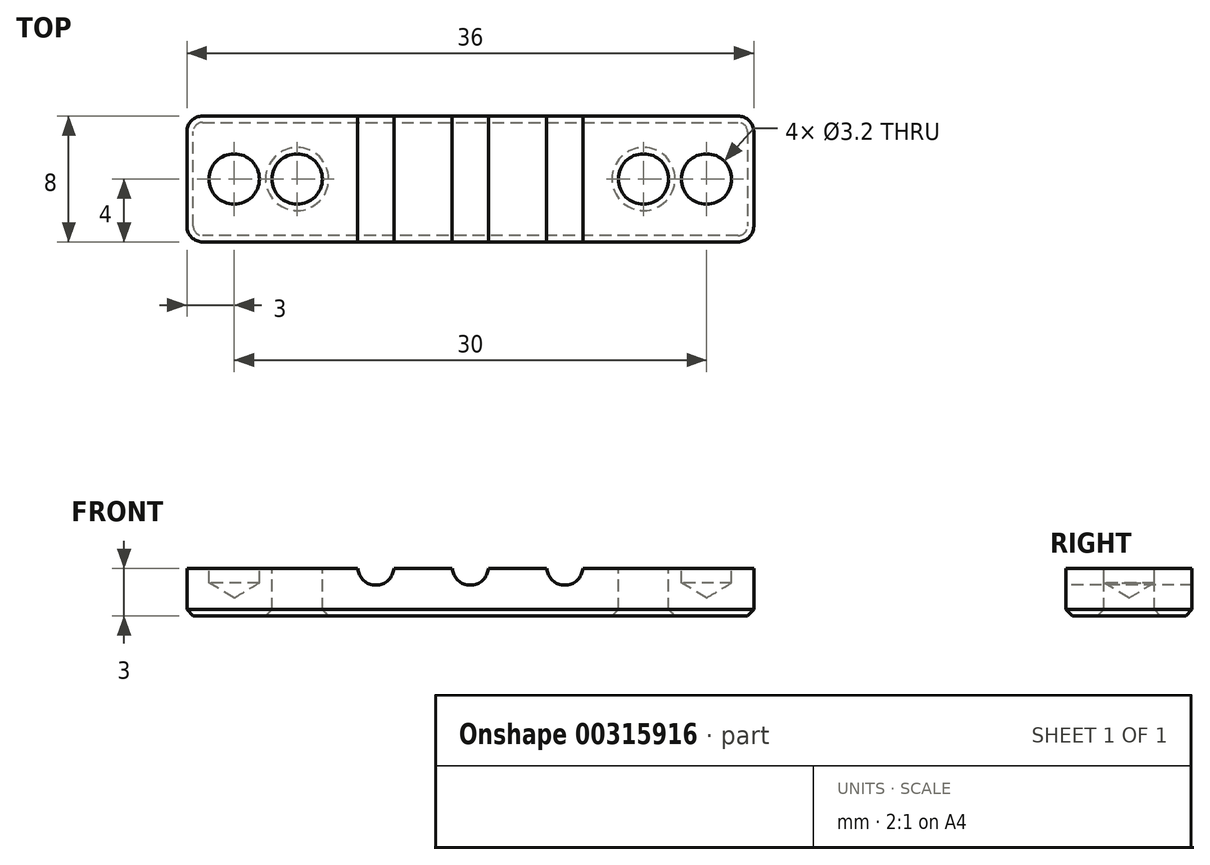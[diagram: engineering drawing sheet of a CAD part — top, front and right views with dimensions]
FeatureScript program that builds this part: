
annotation { "Feature Type Name" : "Feature", "Feature Type Description" : "" }
export const myFeature = defineFeature(function(context is Context, id is Id, definition is map)
    precondition{}
    {
        {
            var Q0;
            Q0=qCreatedBy(makeId("Top.planeOp"),FACE);
            var sketch = newSketch(context, id + "F0", { "sketchPlane" : qUnion([Q0])});
            skLineSegment(sketch, "E0.bottom", {"start": v(3, 4) * mm, "end": v(-3, 4) * mm});
            skLineSegment(sketch, "E0.top", {"start": v(3, -4) * mm, "end": v(-3, -4) * mm});
            skLineSegment(sketch, "E0.left", {"start": v(3, 4) * mm, "end": v(3, -4) * mm});
            skLineSegment(sketch, "E0.right", {"start": v(-3, 4) * mm, "end": v(-3, -4) * mm});
            skPoint(sketch, "E0.middle", {"position": v(0, 0) * mm});
            skLineSegment(sketch, "E1.bottom", {"start": v(33, 4) * mm, "end": v(27, 4) * mm});
            skLineSegment(sketch, "E1.top", {"start": v(33, -4) * mm, "end": v(27, -4) * mm});
            skLineSegment(sketch, "E1.left", {"start": v(33, 4) * mm, "end": v(33, -4) * mm});
            skLineSegment(sketch, "E1.right", {"start": v(27, 4) * mm, "end": v(27, -4) * mm});
            skPoint(sketch, "E1.middle", {"position": v(30, 0) * mm});
            skLineSegment(sketch, "E2", {"start": v(3, 4) * mm, "end": v(27, 4) * mm});
            skLineSegment(sketch, "E3", {"start": v(3, -4) * mm, "end": v(27, -4) * mm});
            skLineSegment(sketch, "E4", {"start": v(9, 4) * mm, "end": v(9, -4) * mm, "construction": true});
            skLineSegment(sketch, "E5.1.0.0", {"start": v(15, 4) * mm, "end": v(15, -4) * mm, "construction": true});
            skLineSegment(sketch, "E5.2.0.0", {"start": v(21, 4) * mm, "end": v(21, -4) * mm, "construction": true});
            skLineSegment(sketch, "E5.direction1", {"start": v(9, -4) * mm, "end": v(15, -4) * mm, "construction": true});
            skPoint(sketch, "E6", {"position": v(4, 0) * mm});
            skPoint(sketch, "E6.positionSnap0", {"position": v(3, 0) * mm});
            skPoint(sketch, "E7", {"position": v(26, 0) * mm});
            skPoint(sketch, "E7.positionSnap0", {"position": v(27, 0) * mm});
            skSolve(sketch);
        }
        {
            var Q0;
            Q0=makeQuery(id+"F0.imprint","IMPRINT",FACE,{"disambiguationData":[TD([[makeQuery(id+"F0.imprint","IMPRINT",EDGE,{"derivedFrom":sQuery(id+"F0.wireOp",EDGE,"E0.bottom")}),1.0]])]});
            var Q1;
            Q1=makeQuery(id+"F0.imprint","IMPRINT",FACE,{"disambiguationData":[TD([[makeQuery(id+"F0.imprint","IMPRINT",EDGE,{"derivedFrom":sQuery(id+"F0.wireOp",EDGE,"E0.left")}),1.0]])]});
            var Q2;
            Q2=makeQuery(id+"F0.imprint","IMPRINT",FACE,{"disambiguationData":[TD([[makeQuery(id+"F0.imprint","IMPRINT",EDGE,{"derivedFrom":sQuery(id+"F0.wireOp",EDGE,"E1.bottom")}),1.0]])]});
            extrude(context, id + "F1", {"entities" : qUnion([Q0, Q1, Q2]), "oppositeDirection" : true, "depth" : 3.1 * mm});
        }
        {
            var Q0;
            Q0=sQuery(id+"F0.wireOp",VERTEX,"E6");
            var Q1;
            Q1=sQuery(id+"F0.wireOp",VERTEX,"E7");
            var Q2;
            Q2=makeQuery(id+"F1.opExtrude","SWEPT_BODY",BODY,{"disambiguationData":[OSD([sQuery(id+"F0.wireOp",EDGE,"E0.bottom"),sQuery(id+"F0.wireOp",EDGE,"E0.top"),sQuery(id+"F0.wireOp",EDGE,"E0.right"),sQuery(id+"F0.wireOp",EDGE,"E1.bottom"),sQuery(id+"F0.wireOp",EDGE,"E1.top"),sQuery(id+"F0.wireOp",EDGE,"E1.left"),sQuery(id+"F0.wireOp",EDGE,"E2"),sQuery(id+"F0.wireOp",EDGE,"E3")])]});
            hole(context, id + "F2", {"style" : HoleStyle.SIMPLE, "endStyle" : HoleEndStyle.THROUGH, "holeDiameter" : 3.2 * mm, "tappedDepth" : 12 * mm, "tapClearance" : 3, "locations" : qUnion([Q0, Q1]), "scope" : qUnion([Q2])});
        }
        {
            var Q0;
            Q0=sQuery(id+"F0.wireOp",VERTEX,"E0.middle");
            var Q1;
            Q1=sQuery(id+"F0.wireOp",VERTEX,"E1.middle");
            var Q2;
            Q2=makeQuery(id+"F1.opExtrude","SWEPT_BODY",BODY,{"disambiguationData":[OSD([sQuery(id+"F0.wireOp",EDGE,"E0.bottom"),sQuery(id+"F0.wireOp",EDGE,"E0.top"),sQuery(id+"F0.wireOp",EDGE,"E0.right"),sQuery(id+"F0.wireOp",EDGE,"E1.bottom"),sQuery(id+"F0.wireOp",EDGE,"E1.top"),sQuery(id+"F0.wireOp",EDGE,"E1.left"),sQuery(id+"F0.wireOp",EDGE,"E2"),sQuery(id+"F0.wireOp",EDGE,"E3")])]});
            hole(context, id + "F3", {"style" : HoleStyle.SIMPLE, "endStyle" : HoleEndStyle.BLIND, "holeDiameter" : 3.2 * mm, "holeDepth" : 1 * mm, "tappedDepth" : 12 * mm, "tapClearance" : 3, "locations" : qUnion([Q0, Q1]), "scope" : qUnion([Q2])});
        }
        {
            var Q0;
            {var subQ0=sQuery(id+"F0.wireOp",EDGE,"E3");var subQ1=sQuery(id+"F0.wireOp",EDGE,"E1.top");var subQ2=sQuery(id+"F0.wireOp",EDGE,"E0.top");Q0=makeQuery(id+"FaaVOSY5iOmgxNq_1.boolean.opBoolean","MERGE",FACE,{"derivedFrom":[makeQuery(id+"F1.opExtrude","SWEPT_FACE",FACE,{"disambiguationData":[OSD([subQ2,subQ1,subQ0])]}),makeQuery(id+"FaaVOSY5iOmgxNq_1.opExtrude","SWEPT_FACE",FACE,{"disambiguationData":[OSD([subQ2,subQ1,subQ0])]})]});}
            var sketch = newSketch(context, id + "F4", { "sketchPlane" : qUnion([Q0])});
            skPoint(sketch, "E8", {"position": v(9, 0) * mm});
            skPoint(sketch, "E9", {"position": v(15, 0) * mm});
            skPoint(sketch, "E10", {"position": v(21, 0) * mm});
            skSolve(sketch);
        }
        {
            var Q0;
            Q0=sQuery(id+"F4.wireOp",VERTEX,"E8");
            var Q1;
            Q1=sQuery(id+"F4.wireOp",VERTEX,"E10");
            var Q2;
            Q2=sQuery(id+"F4.wireOp",VERTEX,"E9");
            var Q3;
            Q3=makeQuery(id+"F1.opExtrude","SWEPT_BODY",BODY,{"disambiguationData":[OSD([sQuery(id+"F0.wireOp",EDGE,"E0.bottom"),sQuery(id+"F0.wireOp",EDGE,"E0.top"),sQuery(id+"F0.wireOp",EDGE,"E0.right"),sQuery(id+"F0.wireOp",EDGE,"E1.bottom"),sQuery(id+"F0.wireOp",EDGE,"E1.top"),sQuery(id+"F0.wireOp",EDGE,"E1.left"),sQuery(id+"F0.wireOp",EDGE,"E2"),sQuery(id+"F0.wireOp",EDGE,"E3")])]});
            hole(context, id + "F5", {"style" : HoleStyle.SIMPLE, "endStyle" : HoleEndStyle.THROUGH, "holeDiameter" : 2.3 * mm, "tappedDepth" : 12 * mm, "tapClearance" : 3, "locations" : qUnion([Q0, Q1, Q2]), "scope" : qUnion([Q3])});
        }
        {
            var Q0;
            Q0=makeQuery(id+"F1.opExtrude","SWEPT_EDGE",EDGE,{"disambiguationData":[OSD([sQuery(id+"F0.wireOp",EDGE,"E0.top"),sQuery(id+"F0.wireOp",EDGE,"E0.right")])]});
            var Q1;
            Q1=makeQuery(id+"F1.opExtrude","SWEPT_EDGE",EDGE,{"disambiguationData":[OSD([sQuery(id+"F0.wireOp",EDGE,"E1.top"),sQuery(id+"F0.wireOp",EDGE,"E1.left")])]});
            var Q2;
            Q2=makeQuery(id+"F1.opExtrude","SWEPT_EDGE",EDGE,{"disambiguationData":[OSD([sQuery(id+"F0.wireOp",EDGE,"E1.bottom"),sQuery(id+"F0.wireOp",EDGE,"E1.left")])]});
            var Q3;
            Q3=makeQuery(id+"F1.opExtrude","SWEPT_EDGE",EDGE,{"disambiguationData":[OSD([sQuery(id+"F0.wireOp",EDGE,"E0.bottom"),sQuery(id+"F0.wireOp",EDGE,"E0.right")])]});
            fillet(context, id + "F6", {"entities" : qUnion([Q0, Q1, Q2, Q3]), "radius" : 1 * mm, "tangentPropagation" : true, "allowEdgeOverflow" : false});
        }
        {
            var Q0;
            Q0=makeQuery(id+"F1.opExtrude","CAP_FACE",FACE,{"disambiguationData":[OSD([sQuery(id+"F0.wireOp",EDGE,"E0.bottom"),sQuery(id+"F0.wireOp",EDGE,"E0.top"),sQuery(id+"F0.wireOp",EDGE,"E0.right"),sQuery(id+"F0.wireOp",EDGE,"E1.bottom"),sQuery(id+"F0.wireOp",EDGE,"E1.top"),sQuery(id+"F0.wireOp",EDGE,"E1.left"),sQuery(id+"F0.wireOp",EDGE,"E2"),sQuery(id+"F0.wireOp",EDGE,"E3")])],"isStart":false});
            chamfer(context, id + "F7", {"entities" : qUnion([Q0]), "width" : 0.4 * mm, "tangentPropagation" : true});
        }
        {
            var Q0;
            {var subQ0=sQuery(id+"F0.wireOp",EDGE,"E0.right");var subQ1=sQuery(id+"F0.wireOp",EDGE,"E3");var subQ2=sQuery(id+"F0.wireOp",EDGE,"E1.top");var subQ3=sQuery(id+"F0.wireOp",EDGE,"E0.top");var subQ4=sQuery(id+"F0.wireOp",EDGE,"E2");var subQ5=sQuery(id+"F0.wireOp",EDGE,"E1.bottom");var subQ6=sQuery(id+"F0.wireOp",EDGE,"E0.bottom");Q0=makeQuery(id+"F5.hole-0.boolean.opBoolean","SPLIT",FACE,{"disambiguationData":[TD([makeQuery(id+"F1.opExtrude","SWEPT_FACE",FACE,{"disambiguationData":[OSD([subQ0])]})])],"derivedFrom":makeQuery(id+"F1.opExtrude","CAP_FACE",FACE,{"disambiguationData":[OSD([subQ6,subQ3,subQ0,subQ5,subQ2,sQuery(id+"F0.wireOp",EDGE,"E1.left"),subQ4,subQ1])],"isStart":true})});}
            var Q1;
            {var subQ0=sQuery(id+"F0.wireOp",EDGE,"E2");var subQ1=sQuery(id+"F0.wireOp",EDGE,"E1.bottom");var subQ2=sQuery(id+"F0.wireOp",EDGE,"E0.bottom");var subQ4=sQuery(id+"F0.wireOp",EDGE,"E3");var subQ5=sQuery(id+"F0.wireOp",EDGE,"E1.top");var subQ6=sQuery(id+"F0.wireOp",EDGE,"E0.top");var subQ8=makeQuery(id+"F5.hole-0.opRevolve","SWEPT_FACE",FACE,{"disambiguationData":[OSD([sQuery(id+"F5.hole-0.sketch.wireOp",EDGE,"core_line_2")])]});var subQ9=makeQuery(id+"F5.hole-0.boolean.opBoolean","COPY",FACE,{"derivedFrom":subQ8});var subQ10=sQuery(id+"F0.wireOp",EDGE,"E1.left");Q1=makeQuery(id+"F5.hole-2.boolean.opBoolean","SPLIT",FACE,{"disambiguationData":[TD([subQ9])],"derivedFrom":makeQuery(id+"F5.hole-1.boolean.opBoolean","SPLIT",FACE,{"disambiguationData":[TD([subQ9])],"derivedFrom":makeQuery(id+"F5.hole-0.boolean.opBoolean","SPLIT",FACE,{"disambiguationData":[TD([makeQuery(id+"F1.opExtrude","SWEPT_FACE",FACE,{"disambiguationData":[OSD([subQ10])]})])],"derivedFrom":makeQuery(id+"F1.opExtrude","CAP_FACE",FACE,{"disambiguationData":[OSD([subQ2,subQ6,sQuery(id+"F0.wireOp",EDGE,"E0.right"),subQ1,subQ5,subQ10,subQ0,subQ4])],"isStart":true})})})});}
            var Q2;
            {var subQ0=sQuery(id+"F0.wireOp",EDGE,"E2");var subQ1=sQuery(id+"F0.wireOp",EDGE,"E1.bottom");var subQ2=sQuery(id+"F0.wireOp",EDGE,"E0.bottom");var subQ4=sQuery(id+"F0.wireOp",EDGE,"E3");var subQ5=sQuery(id+"F0.wireOp",EDGE,"E1.top");var subQ6=sQuery(id+"F0.wireOp",EDGE,"E0.top");var subQ8=makeQuery(id+"F5.hole-1.opRevolve","SWEPT_FACE",FACE,{"disambiguationData":[OSD([sQuery(id+"F5.hole-1.sketch.wireOp",EDGE,"core_line_2")])]});var subQ9=makeQuery(id+"F5.hole-0.opRevolve","SWEPT_FACE",FACE,{"disambiguationData":[OSD([sQuery(id+"F5.hole-0.sketch.wireOp",EDGE,"core_line_2")])]});var subQ10=sQuery(id+"F0.wireOp",EDGE,"E1.left");Q2=makeQuery(id+"F5.hole-2.boolean.opBoolean","SPLIT",FACE,{"disambiguationData":[TD([makeQuery(id+"F5.hole-1.boolean.opBoolean","COPY",FACE,{"derivedFrom":subQ8})])],"derivedFrom":makeQuery(id+"F5.hole-1.boolean.opBoolean","SPLIT",FACE,{"disambiguationData":[TD([makeQuery(id+"F5.hole-0.boolean.opBoolean","COPY",FACE,{"derivedFrom":subQ9})])],"derivedFrom":makeQuery(id+"F5.hole-0.boolean.opBoolean","SPLIT",FACE,{"disambiguationData":[TD([makeQuery(id+"F1.opExtrude","SWEPT_FACE",FACE,{"disambiguationData":[OSD([subQ10])]})])],"derivedFrom":makeQuery(id+"F1.opExtrude","CAP_FACE",FACE,{"disambiguationData":[OSD([subQ2,subQ6,sQuery(id+"F0.wireOp",EDGE,"E0.right"),subQ1,subQ5,subQ10,subQ0,subQ4])],"isStart":true})})})});}
            var Q3;
            {var subQ1=sQuery(id+"F0.wireOp",EDGE,"E3");var subQ2=sQuery(id+"F0.wireOp",EDGE,"E1.top");var subQ3=sQuery(id+"F0.wireOp",EDGE,"E0.top");var subQ5=sQuery(id+"F0.wireOp",EDGE,"E1.left");var subQ6=makeQuery(id+"F1.opExtrude","SWEPT_FACE",FACE,{"disambiguationData":[OSD([subQ5])]});var subQ7=sQuery(id+"F0.wireOp",EDGE,"E2");var subQ8=sQuery(id+"F0.wireOp",EDGE,"E1.bottom");var subQ9=sQuery(id+"F0.wireOp",EDGE,"E0.bottom");Q3=makeQuery(id+"F5.hole-1.boolean.opBoolean","SPLIT",FACE,{"disambiguationData":[TD([subQ6])],"derivedFrom":makeQuery(id+"F5.hole-0.boolean.opBoolean","SPLIT",FACE,{"disambiguationData":[TD([subQ6])],"derivedFrom":makeQuery(id+"F1.opExtrude","CAP_FACE",FACE,{"disambiguationData":[OSD([subQ9,subQ3,sQuery(id+"F0.wireOp",EDGE,"E0.right"),subQ8,subQ2,subQ5,subQ7,subQ1])],"isStart":true})})});}
            extrude(context, id + "F8", {"entities" : qUnion([Q0, Q1, Q2, Q3]), "operationType" : NewBodyOperationType.REMOVE, "oppositeDirection" : true, "depth" : 0.1 * mm});
        }
    });
